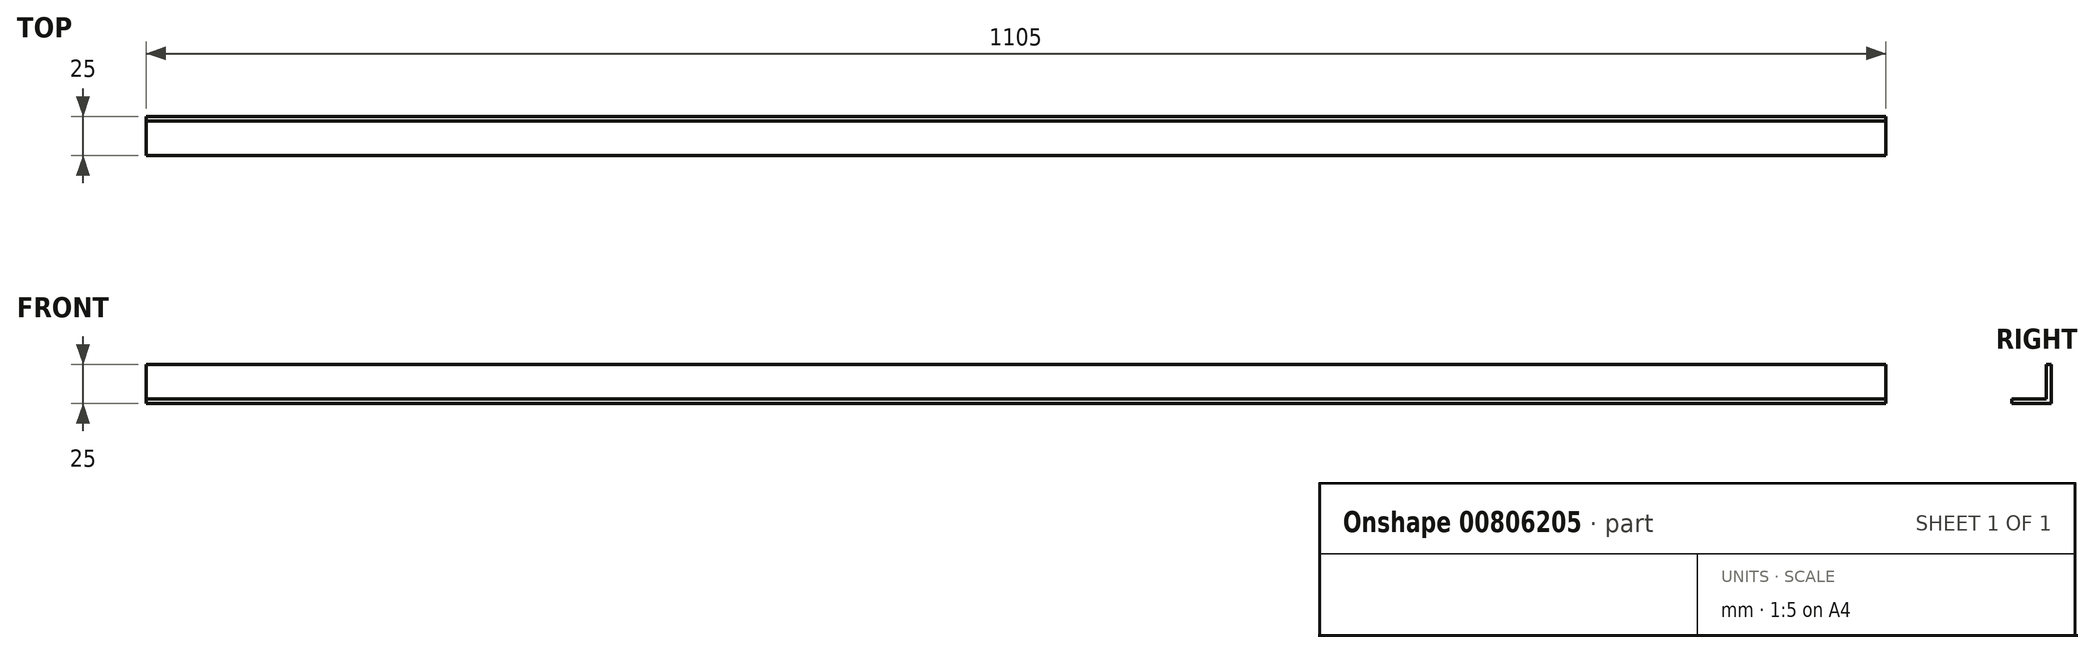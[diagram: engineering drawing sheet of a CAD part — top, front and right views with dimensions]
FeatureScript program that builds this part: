
annotation { "Feature Type Name" : "Feature", "Feature Type Description" : "" }
export const myFeature = defineFeature(function(context is Context, id is Id, definition is map)
    precondition{}
    {
        {
            var Q0;
            Q0=qCreatedBy(makeId("Right.planeOp"),FACE);
            var sketch = newSketch(context, id + "F0", { "sketchPlane" : qUnion([Q0])});
            skLineSegment(sketch, "E0", {"start": v(0, 0) * mm, "end": v(0, 25) * mm});
            skLineSegment(sketch, "E1", {"start": v(0, 0) * mm, "end": v(-25, 0) * mm});
            skLineSegment(sketch, "E2.0", {"start": v(-3, 3) * mm, "end": v(-3, 25) * mm});
            skLineSegment(sketch, "E2.1", {"start": v(-3, 3) * mm, "end": v(-25, 3) * mm});
            skLineSegment(sketch, "E3", {"start": v(0, 25) * mm, "end": v(-3, 25) * mm});
            skLineSegment(sketch, "E4", {"start": v(-25, 0) * mm, "end": v(-25, 3) * mm});
            skSolve(sketch);
        }
        {
            var Q0;
            Q0=qSketchRegion(id+"F0",true);
            extrude(context, id + "F1", {"entities" : qUnion([Q0]), "depth" : 1105 * mm, "offsetDistance" : 25 * mm});
        }
    });
